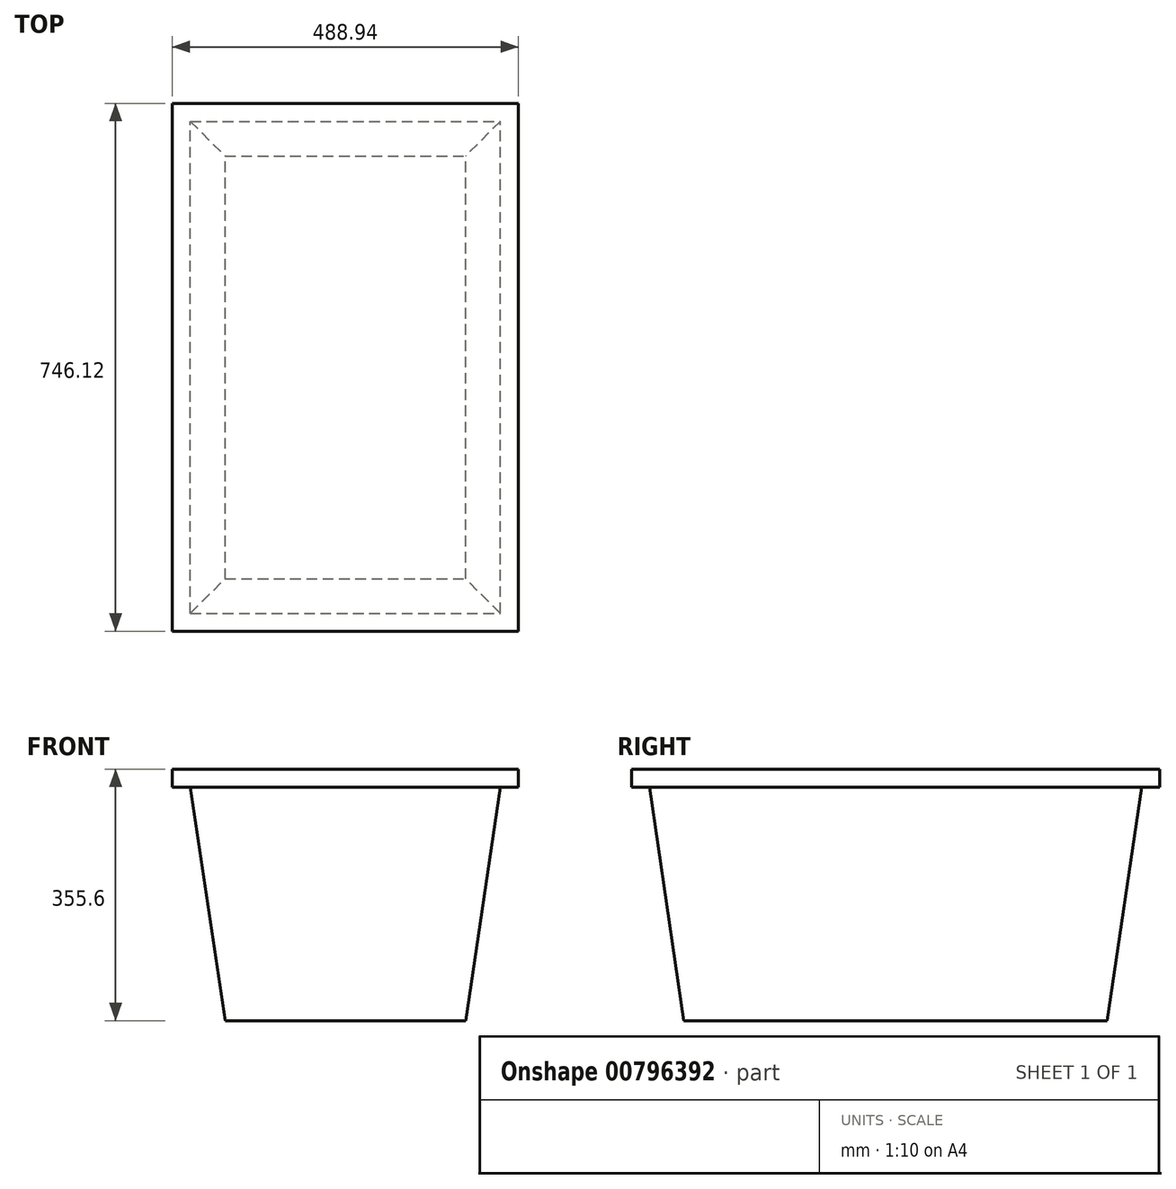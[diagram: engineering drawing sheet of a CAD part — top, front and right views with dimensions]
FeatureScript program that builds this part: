
annotation { "Feature Type Name" : "Feature", "Feature Type Description" : "" }
export const myFeature = defineFeature(function(context is Context, id is Id, definition is map)
    precondition{}
    {
        {
            var Q0;
            Q0=qCreatedBy(makeId("Front.planeOp"),FACE);
            var sketch = newSketch(context, id + "F0", { "sketchPlane" : qUnion([Q0])});
            skLineSegment(sketch, "E0.bottom", {"start": v(-219.08, 76.2) * mm, "end": v(219.08, 76.2) * mm});
            skLineSegment(sketch, "E0.top", {"start": v(-169.86, -254) * mm, "end": v(169.86, -254) * mm});
            skLineSegment(sketch, "E0.left", {"start": v(-219.08, 76.2) * mm, "end": v(-169.86, -254) * mm});
            skLineSegment(sketch, "E0.right", {"start": v(219.08, 76.2) * mm, "end": v(169.86, -254) * mm});
            skLineSegment(sketch, "E1.bottom", {"start": v(-244.48, 101.6) * mm, "end": v(244.47, 101.6) * mm});
            skLineSegment(sketch, "E1.top", {"start": v(-244.48, 76.2) * mm, "end": v(244.47, 76.2) * mm});
            skLineSegment(sketch, "E1.left", {"start": v(-244.48, 101.6) * mm, "end": v(-244.48, 76.2) * mm});
            skLineSegment(sketch, "E1.right", {"start": v(244.47, 101.6) * mm, "end": v(244.47, 76.2) * mm});
            skSolve(sketch);
        }
        {
            var Q0;
            Q0=makeQuery(id+"F0.imprint","IMPRINT",FACE,{"disambiguationData":[TD([[makeQuery(id+"F0.imprint","IMPRINT",EDGE,{"derivedFrom":sQuery(id+"F0.wireOp",EDGE,"E0.bottom")}),-1.0]])]});
            var Q1;
            {var subQ1=sQuery(id+"F0.wireOp",EDGE,"E0.bottom");Q1=makeQuery(id+"F0.imprint","IMPRINT",FACE,{"disambiguationData":[TD([[makeQuery(id+"F0.imprint","IMPRINT",EDGE,{"derivedFrom":subQ1}),1.0]])]});}
            extrude(context, id + "F1", {"entities" : qUnion([Q0, Q1]), "depth" : 746.12 * mm, "offsetDistance" : 25.4 * mm});
        }
        {
            var Q0;
            Q0=makeQuery(id+"F1.opExtrude","SWEPT_FACE",FACE,{"disambiguationData":[OSD([sQuery(id+"F0.wireOp",EDGE,"E1.right")])]});
            var sketch = newSketch(context, id + "F2", { "sketchPlane" : qUnion([Q0])});
            skLineSegment(sketch, "E2", {"start": v(-746.12, 76.2) * mm, "end": v(-720.73, 76.2) * mm});
            skLineSegment(sketch, "E3", {"start": v(-720.73, 76.2) * mm, "end": v(-671.5, -258.8) * mm});
            skLineSegment(sketch, "E4", {"start": v(-671.5, -258.8) * mm, "end": v(-746.12, -258.8) * mm});
            skLineSegment(sketch, "E5", {"start": v(-746.12, -258.8) * mm, "end": v(-746.12, 76.2) * mm});
            skLineSegment(sketch, "E6", {"start": v(0, 76.2) * mm, "end": v(-25.4, 76.2) * mm});
            skLineSegment(sketch, "E7", {"start": v(-25.4, 76.2) * mm, "end": v(-74.63, -255.17) * mm});
            skLineSegment(sketch, "E8", {"start": v(-74.63, -255.17) * mm, "end": v(0, -255.17) * mm});
            skLineSegment(sketch, "E9", {"start": v(0, -255.17) * mm, "end": v(0, 76.2) * mm});
            skSolve(sketch);
        }
        {
            var Q0;
            Q0 = qSketchRegion(id + "F2", true);
            extrude(context, id + "F3", {"entities" : qUnion([Q0]), "operationType" : NewBodyOperationType.REMOVE, "oppositeDirection" : true, "depth" : 1270 * mm, "offsetDistance" : 25.4 * mm});
        }
    });
